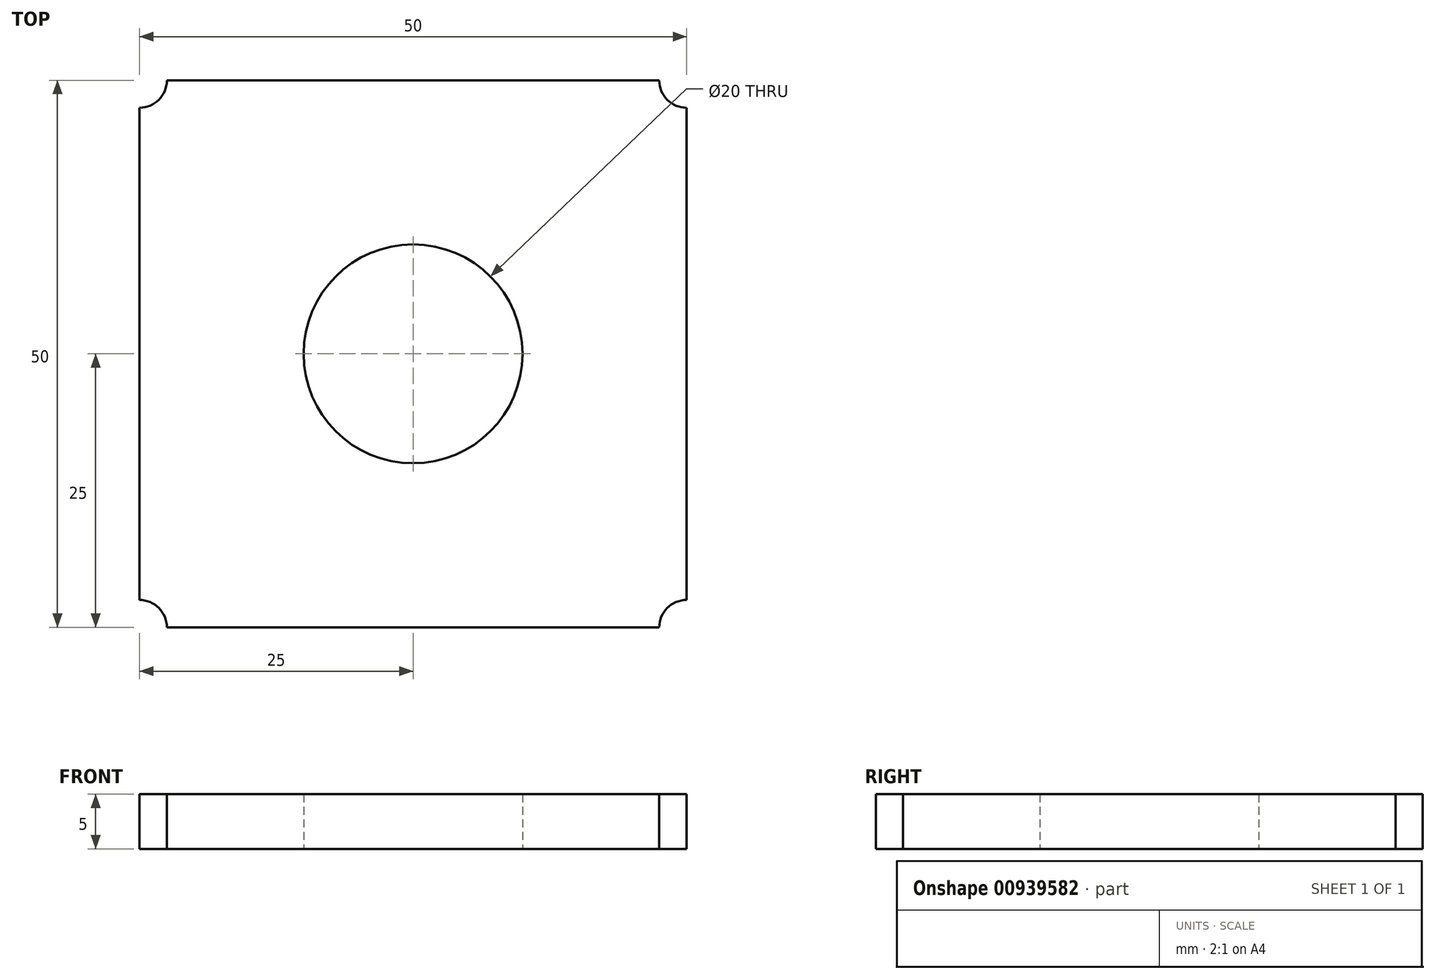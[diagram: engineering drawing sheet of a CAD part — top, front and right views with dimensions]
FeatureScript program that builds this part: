
annotation { "Feature Type Name" : "Feature", "Feature Type Description" : "" }
export const myFeature = defineFeature(function(context is Context, id is Id, definition is map)
    precondition{}
    {
        {
            var Q0;
            Q0=qCreatedBy(makeId("Top.planeOp"),FACE);
            var sketch = newSketch(context, id + "F0", { "sketchPlane" : qUnion([Q0])});
            skLineSegment(sketch, "E0.bottom", {"start": v(-22.5, -25) * mm, "end": v(22.5, -25) * mm});
            skLineSegment(sketch, "E0.top", {"start": v(-22.5, 25) * mm, "end": v(22.5, 25) * mm});
            skLineSegment(sketch, "E0.left", {"start": v(-25, -22.5) * mm, "end": v(-25, 22.5) * mm});
            skLineSegment(sketch, "E0.right", {"start": v(25, -22.5) * mm, "end": v(25, 22.5) * mm});
            skPoint(sketch, "E0.middle", {"position": v(0, 0) * mm});
            skArc(sketch, "E1", {"start": v(22.5, 25) * mm, "mid": v(23.23, 23.23) * mm, "end": v(25, 22.5) * mm});
            skArc(sketch, "E2", {"start": v(-25, 22.5) * mm, "mid": v(-23.23, 23.23) * mm, "end": v(-22.5, 25) * mm});
            skArc(sketch, "E3", {"start": v(-22.5, -25) * mm, "mid": v(-23.23, -23.23) * mm, "end": v(-25, -22.5) * mm});
            skArc(sketch, "E4", {"start": v(25, -22.5) * mm, "mid": v(23.23, -23.23) * mm, "end": v(22.5, -25) * mm});
            skCircle(sketch, "E5", {"center": v(0, 0) * mm, "radius": 10 * mm});
            skSolve(sketch);
        }
        {
            var Q0;
            Q0=makeQuery(id+"F0.imprint","IMPRINT",FACE,{"disambiguationData":[TD([[makeQuery(id+"F0.imprint","IMPRINT",EDGE,{"derivedFrom":sQuery(id+"F0.wireOp",EDGE,"E0.bottom")}),1.0]])]});
            extrude(context, id + "F1", {"entities" : qUnion([Q0]), "depth" : 5 * mm, "offsetDistance" : 25 * mm});
        }
    });
